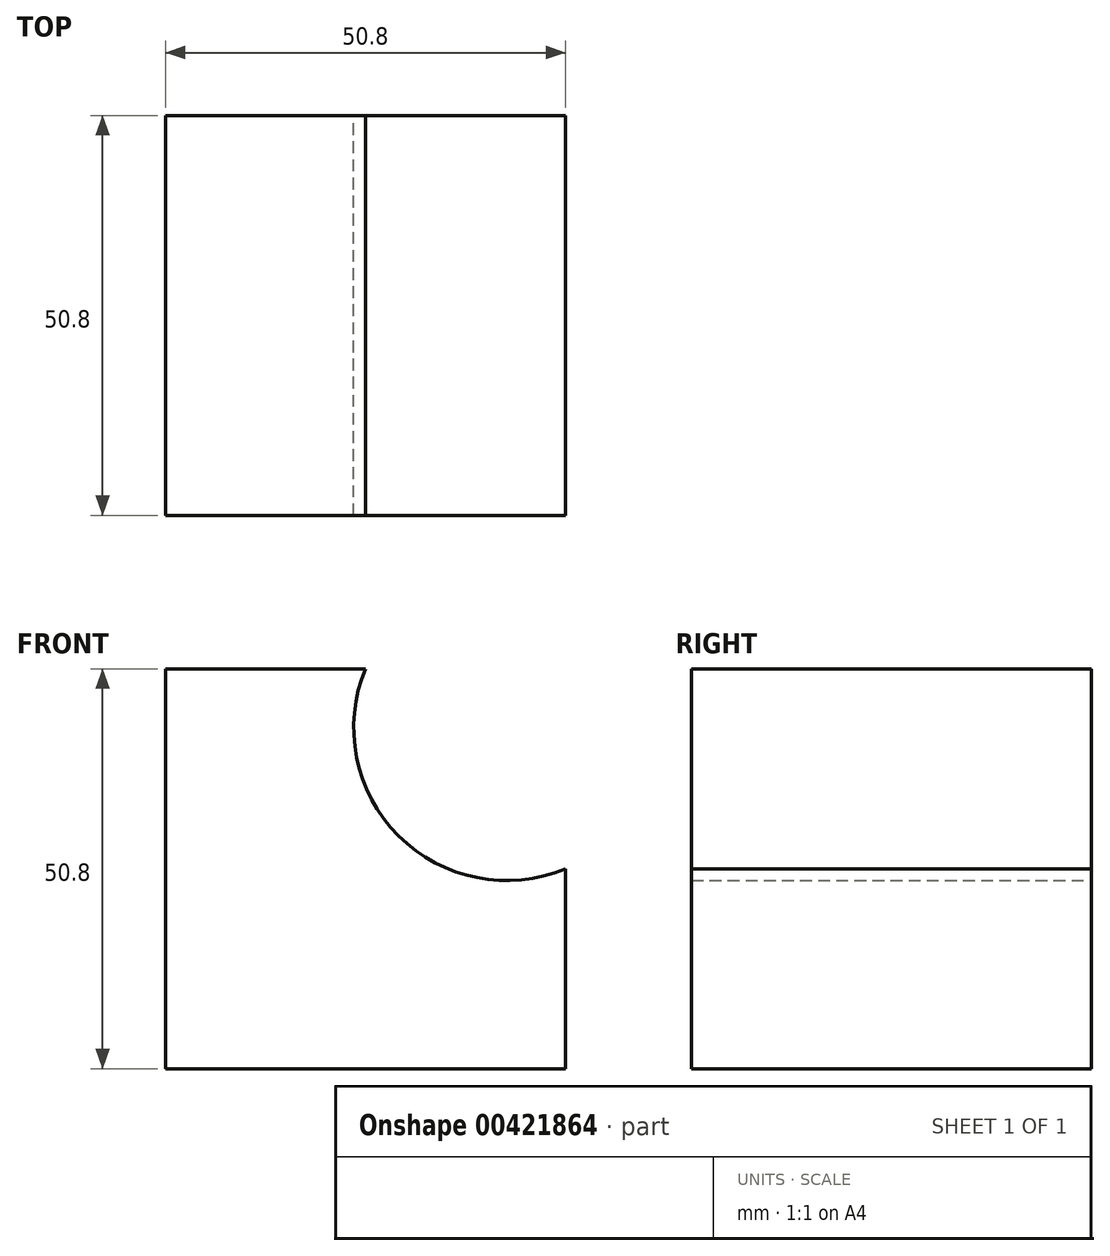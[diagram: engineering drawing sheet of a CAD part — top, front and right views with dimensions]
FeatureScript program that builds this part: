
annotation { "Feature Type Name" : "Feature", "Feature Type Description" : "" }
export const myFeature = defineFeature(function(context is Context, id is Id, definition is map)
    precondition{}
    {
        {
            var Q0;
            Q0=qCreatedBy(makeId("Front.planeOp"),FACE);
            var sketch = newSketch(context, id + "F0", { "sketchPlane" : qUnion([Q0])});
            skLineSegment(sketch, "E0", {"start": v(-25.4, 54.55) * mm, "end": v(0, 54.55) * mm});
            skLineSegment(sketch, "E1", {"start": v(-25.4, 54.55) * mm, "end": v(-25.4, 3.75) * mm});
            skLineSegment(sketch, "E2", {"start": v(-25.4, 3.75) * mm, "end": v(25.4, 3.75) * mm});
            skLineSegment(sketch, "E3", {"start": v(25.4, 3.75) * mm, "end": v(25.4, 29.15) * mm});
            skArc(sketch, "E4", {"start": v(0, 54.55) * mm, "mid": v(4.18, 33.33) * mm, "end": v(25.4, 29.15) * mm});
            skSolve(sketch);
        }
        {
            var Q0;
            Q0=makeQuery(id+"F0.imprint","IMPRINT",FACE,{"disambiguationData":[TD([[makeQuery(id+"F0.imprint","IMPRINT",EDGE,{"derivedFrom":sQuery(id+"F0.wireOp",EDGE,"E0")}),-1.0]])]});
            extrude(context, id + "F1", {"entities" : qUnion([Q0]), "depth" : 50.8 * mm});
        }
    });
